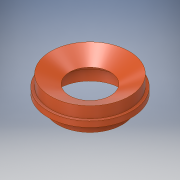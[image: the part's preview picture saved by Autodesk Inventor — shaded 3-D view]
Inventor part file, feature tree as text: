
AUTODESK INVENTOR PART (.ipt)
format: ipt  version: 2017 SP1 (Build 210196100, 196)  size: 170,496 bytes
history: native  units: in
note: dims shown in document units (in); Inventor stores cm internally (conversion verified against a paired STEP export)
features: revolve x1, sketch x1
ambient origin geometry x8: Origin, YZ Plane, XZ Plane, XY Plane, X Axis, Y Axis, Z Axis, Center Point
bodies: Solid1 (feature_tree)
feature tree (2):
  revolve  "Revolution1"  [1 undecoded]
  sketch  "Sketch1"  dims[d0=0.5in d1=1.13in d3=15.0deg d4=0.25in d9=1.5in d11=0.5in d13=3.75in d14=0.25in d15=1.0in d16=0.25in d17=0.5in d18=0.234in d19=0.234in d20=0.5in d22=4.25in d23=2.5in d25=1.0in d26=0.25in d27=5.25in d28=0.125in d29=4.0in d30=0.25in d31=0.1718in d32=1.75in d33=0.125in d34=0.801in d35=0.375in d37=90.0deg]
note: 1 required parameter value undecoded (feature->parameter linkage not recoverable at this tier; creation-order binding heuristic only, values carry confidence <= 0.55)
